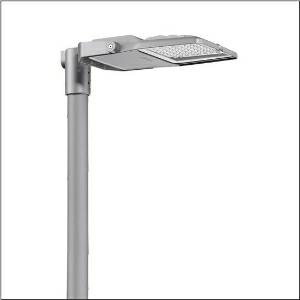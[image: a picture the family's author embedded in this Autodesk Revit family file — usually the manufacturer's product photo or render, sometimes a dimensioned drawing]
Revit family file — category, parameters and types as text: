
# Revit family: floodlight_fl_21_mini___pl33t_5xa7776c2f3a_ca81
name_source: partatom
category: Lighting Fixtures
units: mm (PartAtom-declared; Revit-internal decimal feet)

## family parameters
Cut with Voids When Loaded = No
Host = Face
Light Source = No
Part Type = Normal
Room Calculation Point = No
Round Connector Dimension = Use Diameter
Shared = No

## types (1)
- --- (1 x LED, 12050 lm, 89 W, 3000K)
    Apparent Load = 89 VA
    CIE Flux Codes = 26 75 99 100 100
    Color Rendering = 70
    Color Temperature = 3000K
    Default Elevation = 1800 mm
    Description = Floodlight FL 21 mini, floodlight, primary light control with lens, of PMMA, primary optical cover: protective disc, of toughened safety glass, transparent, light distribution: PL33T, light emission: direct distribution, installation type: surface-mounted, LED, High Power LED, rated luminous flux: 12.050lm, luminous efficacy: 135lm/W, light colour: 730, colour temperature: 3000K, control gear: Smart Interface (Zhaga), control: flexible luminous flux parameterisation, time-dependent luminous flux control, constant luminous flux control, overheat protection, pre-setting: logarithmic dimming characteristic, with terminal, 6-pole, mains connection: 220..240V, AC, 50/60Hz, start of lifetime: 89W, end of service life: 94W, reduction: 43W, luminaire housing, of diecast aluminium, powder-coated, SITECO metallic grey (DB 702S), corrosivity category C5 mid according to DIN EN ISO 12944, suitable for swimming pools, chlorine-resistant, sealing non-destructively replaceable, please order mast flange separately, mast bracket, of steel, galvanised, powder-coated, SITECO metallic grey (DB 702S), Smart Interface below and above, protection rating (complete): IP66, insulation class (complete): insulation class II (safety insulation), certification: CE, ENEC, VDE, protection symbol: D, impact resistance: IK08, permissible operating ambient temperature: -40..+40°C, permissible operating ambient temperature for outdoor applications: -40..+50°C, standard: DIN EN 12944, LABS conformity tested according to VDMA 24364:2018-05, packaging unit: 1 piece

Light Distribution: PL33T
    Height = 70 mm
    Lamp = 1 x LED
    Lamp Light Flux = 12050 lm
    Lamp Power = 89 W
    Lamp count = 1
    Length = 485 mm
    Luminous efficacy = 135 lm/W
    Manufacturer = Siteco
    ModVariant = No
    Model = 5XA7776C2F3A
    Number of Poles = 1
    OnlyDefault = Yes
    Power Factor = 1
    Product Name = Floodlight FL 21 mini | PL33T
    Product group = floodlight | pylon annexe
    ProductGroupID = 6201
    Protection Class = Protection class II
    Protection Degree = IP 66
    RLX_Detail_Level = 1
    RLX_Emergency_Light_Flux = 0 lm
    RLX_Emergency_Type = 0
    RLX_Emergency_Type_DB = No
    RlxData = <blob elided: 100969 chars, md5=a699b189>
    Socket = socket
    Standby Power = 0 W
    System Light Flux = 12050 lm
    System Power = 89 W
    Type Comments = factory setting: luminous flux: 100 % | dim-lin: 254 | 456 mA
    Type Image = l_1007125.jpg
    URL = http://relux.com
    VarID = @adj_147965
    Voltage = 0 V
    Weight = 0.00 kg
    Width = 337 mm

## geometry (parser evidence)
native form markers: Blend x4, Sweep x12
no freeform markers — native parametric forms only
